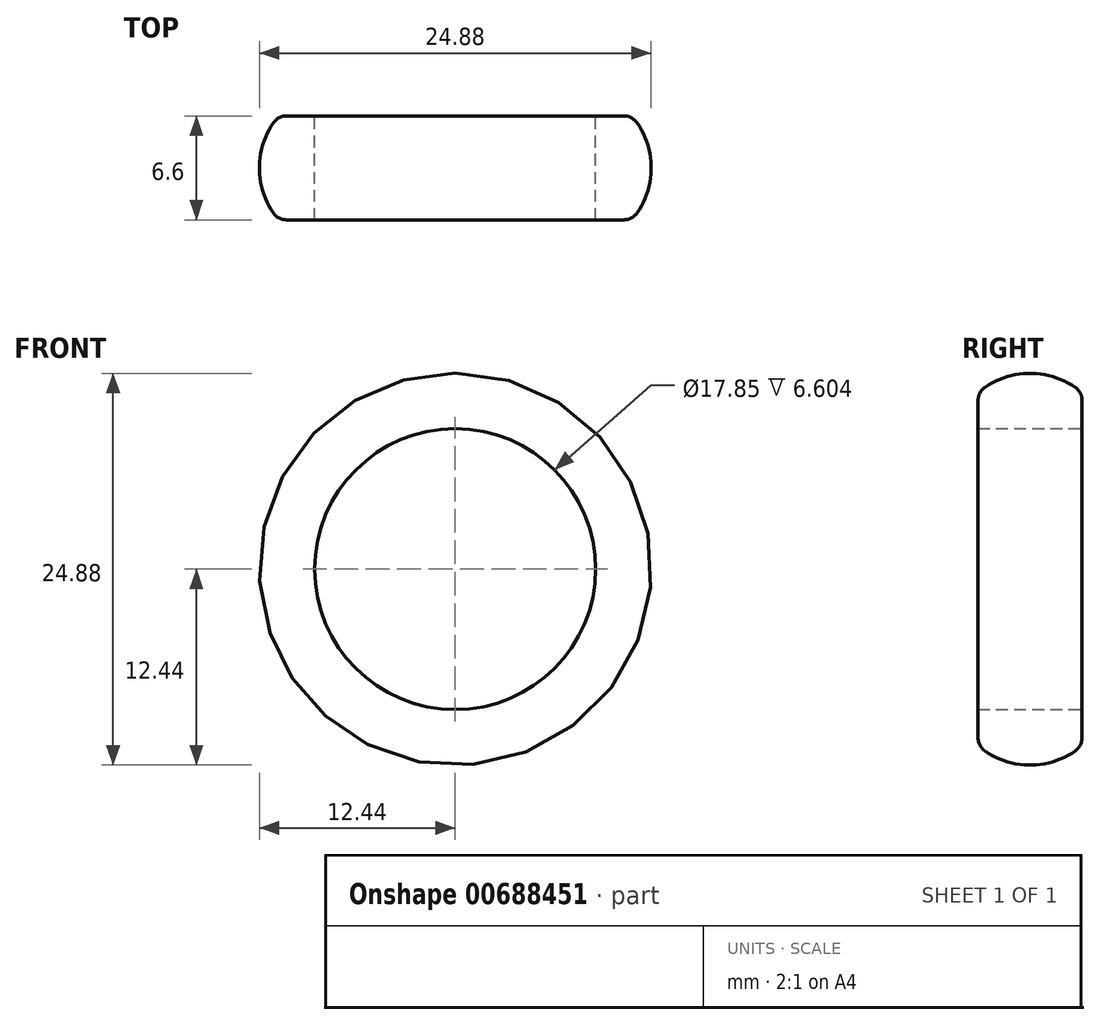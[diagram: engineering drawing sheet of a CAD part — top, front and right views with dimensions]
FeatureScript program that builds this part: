
annotation { "Feature Type Name" : "Feature", "Feature Type Description" : "" }
export const myFeature = defineFeature(function(context is Context, id is Id, definition is map)
    precondition{}
    {
        {
            var Q0;
            Q0=qCreatedBy(makeId("Top.planeOp"),FACE);
            var sketch = newSketch(context, id + "F0", { "sketchPlane" : qUnion([Q0])});
            skPoint(sketch, "E0", {"position": v(0, 0) * mm});
            skLineSegment(sketch, "E1", {"start": v(-8.92, 3.3) * mm, "end": v(-8.92, -3.3) * mm});
            skLineSegment(sketch, "E2", {"start": v(-8.92, -3.3) * mm, "end": v(-11.2, -3.3) * mm});
            skLineSegment(sketch, "E3", {"start": v(-8.92, 3.3) * mm, "end": v(-11.2, 3.3) * mm});
            skArc(sketch, "E4", {"start": v(-11.2, 3.3) * mm, "mid": v(-12.44, 0) * mm, "end": v(-11.2, -3.3) * mm});
            skLineSegment(sketch, "E5", {"start": v(0, 0) * mm, "end": v(-32.5, 0) * mm, "construction": true});
            skPoint(sketch, "E6", {"position": v(-8.92, 0) * mm});
            skLineSegment(sketch, "E7", {"start": v(-11.2, 3.3) * mm, "end": v(-11.2, -27.2) * mm, "construction": true});
            skLineSegment(sketch, "E8", {"start": v(0, 0) * mm, "end": v(0, -6.2) * mm});
            skSolve(sketch);
        }
        {
            var Q0;
            Q0=makeQuery(id+"F0.imprint","IMPRINT",FACE,{"disambiguationData":[TD([[makeQuery(id+"F0.imprint","IMPRINT",EDGE,{"derivedFrom":sQuery(id+"F0.wireOp",EDGE,"E1")}),-1.0]])]});
            var Q1;
            Q1=sQuery(id+"F0.wireOp",EDGE,"E8");
            revolve(context, id + "F1", {"entities" : qUnion([Q0]), "axis" : qUnion([Q1]), "revolveType" : RevolveType.FULL});
        }
        {
            var Q0;
            Q0=makeQuery(id+"F1.opRevolve","SWEPT_EDGE",EDGE,{"disambiguationData":[OSD([sQuery(id+"F0.wireOp",EDGE,"E2"),sQuery(id+"F0.wireOp",EDGE,"E4")])]});
            var Q1;
            Q1=makeQuery(id+"F1.opRevolve","SWEPT_EDGE",EDGE,{"disambiguationData":[OSD([sQuery(id+"F0.wireOp",EDGE,"E3"),sQuery(id+"F0.wireOp",EDGE,"E4")])]});
            fillet(context, id + "F2", {"entities" : qUnion([Q0, Q1]), "radius" : 1.02 * mm, "tangentPropagation" : true, "allowEdgeOverflow" : false});
        }
    });
